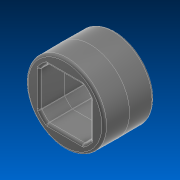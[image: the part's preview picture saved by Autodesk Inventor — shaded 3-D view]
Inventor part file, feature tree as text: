
AUTODESK INVENTOR PART (.ipt)
format: ipt  version: 2022.2 (Build 262287000, 287)  size: 211,968 bytes
history: native  units: in
note: dims shown in document units (in); Inventor stores cm internally (conversion verified against a paired STEP export)
features: fillet x1
ambient origin geometry x8: Origin, YZ Plane, XZ Plane, XY Plane, X Axis, Y Axis, Z Axis, Center Point
bodies: Solid1 (feature_tree)
feature tree (1):
  fillet  "Fillet1"  [1 undecoded]
note: 1 required parameter value undecoded (feature->parameter linkage not recoverable at this tier; creation-order binding heuristic only, values carry confidence <= 0.55)
